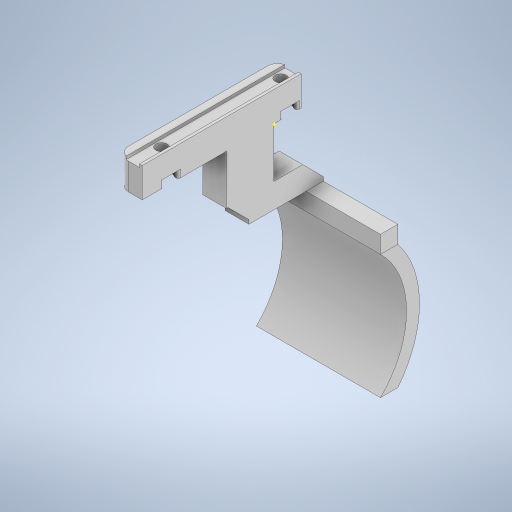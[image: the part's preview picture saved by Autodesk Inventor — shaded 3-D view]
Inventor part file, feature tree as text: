
AUTODESK INVENTOR PART (.ipt)
format: ipt  version: 2024 (Build 280153000, 153)  size: 379,392 bytes
history: native  units: in
note: dims shown in document units (in); Inventor stores cm internally (conversion verified against a paired STEP export)
features: sketch x10, extrude x7, projected_geometry x4, fillet x2, chamfer x2, sweep x1
ambient origin geometry x8: Origin, YZ Plane, XZ Plane, XY Plane, X Axis, Y Axis, Z Axis, Center Point
bodies: Solid1 (feature_tree), Solid2 (feature_tree)
feature tree (26):
  extrude  "Extrusion1"  Depth=2.5197in
  extrude  "Extrusion2"  Depth=1.8898in
  extrude  "Extrusion3"  Depth=0.4724in TaperAngle=0.0deg
  fillet  "Fillet1"  Radius=0.0433in
  fillet  "Fillet2"  Radius=0.2126in
  extrude  "Extrusion19"  Depth=0.4724in TaperAngle=0.0deg
  extrude  "Extrusion21"  Depth=0.1181in TaperAngle=0.0deg
  sketch  "Sketch41"  dims[d17=0.1772in d18=0.0394in]
  extrude  "Extrusion22"  Depth=0.0394in
  sweep  "Sweep4"
  extrude  "Extrusion24"  Depth=0.748in
  chamfer  "Chamfer4"  Distance=0.7874in
  chamfer  "Chamfer5"  Distance=0.3937in
  sketch  "Sketch1"  dims[d1=0.374in d2=2.5197in]
  sketch  "Sketch2"  dims[d3=0.1772in d4=1.8898in]
  sketch  "Sketch3"  dims[d6=0.1457in d7=0.4724in d8=0.0in d9=0.0433in d10=0.2126in]
  projected_geometry  "Projected Loop2"
  projected_geometry  "Projected Loop3"
  projected_geometry  "Projected Loop4"
  projected_geometry  "Projected Loop5"
  sketch  "Sketch28"  dims[d11=0.0472in d12=0.4724in d13=0.0in]
  sketch  "Sketch40"  dims[d14=0.2953in d15=0.1181in d16=0.0in]
  sketch  "Sketch42"  dims[d19=0.1575in d76=0.4724in]
  sketch  "Sketch50"  dims[d107=0.102in d108=0.748in d109=0.7874in d110=0.0in]
  sketch  "Sketch51"  dims[d130=0.7874in]
  sketch  "Sketch57"  dims[d131=1.1811in d132=0.3937in d133=0.0in d134=1.1811in d135=0.2756in d137=1.9685in d138=0.2756in d139=0.0in d147=1.9685in d148=1.378in d149=0.0in d150=0.0in d154=3.8563in d155=0.0in d156=0.3287in d157=0.0787in d158=45.0deg d159=0.3287in d160=0.0787in d161=45.0deg d42=0.0197in d43=0.0344in d44=0.0197in d45=0.0344in d46=0.0in d47=0.0in d48=0.0in d49=0.0in d50=0.0in d51=0.0in d52=0.0in d53=0.0in d55=0.0197in d56=0.0344in d57=0.0197in d58=0.0344in d60=0.0197in d61=0.0344in d62=0.0197in d63=0.0344in d72=0.0197in d73=0.0344in d74=0.0197in d75=0.0344in d140=0.0197in d141=0.0344in]
